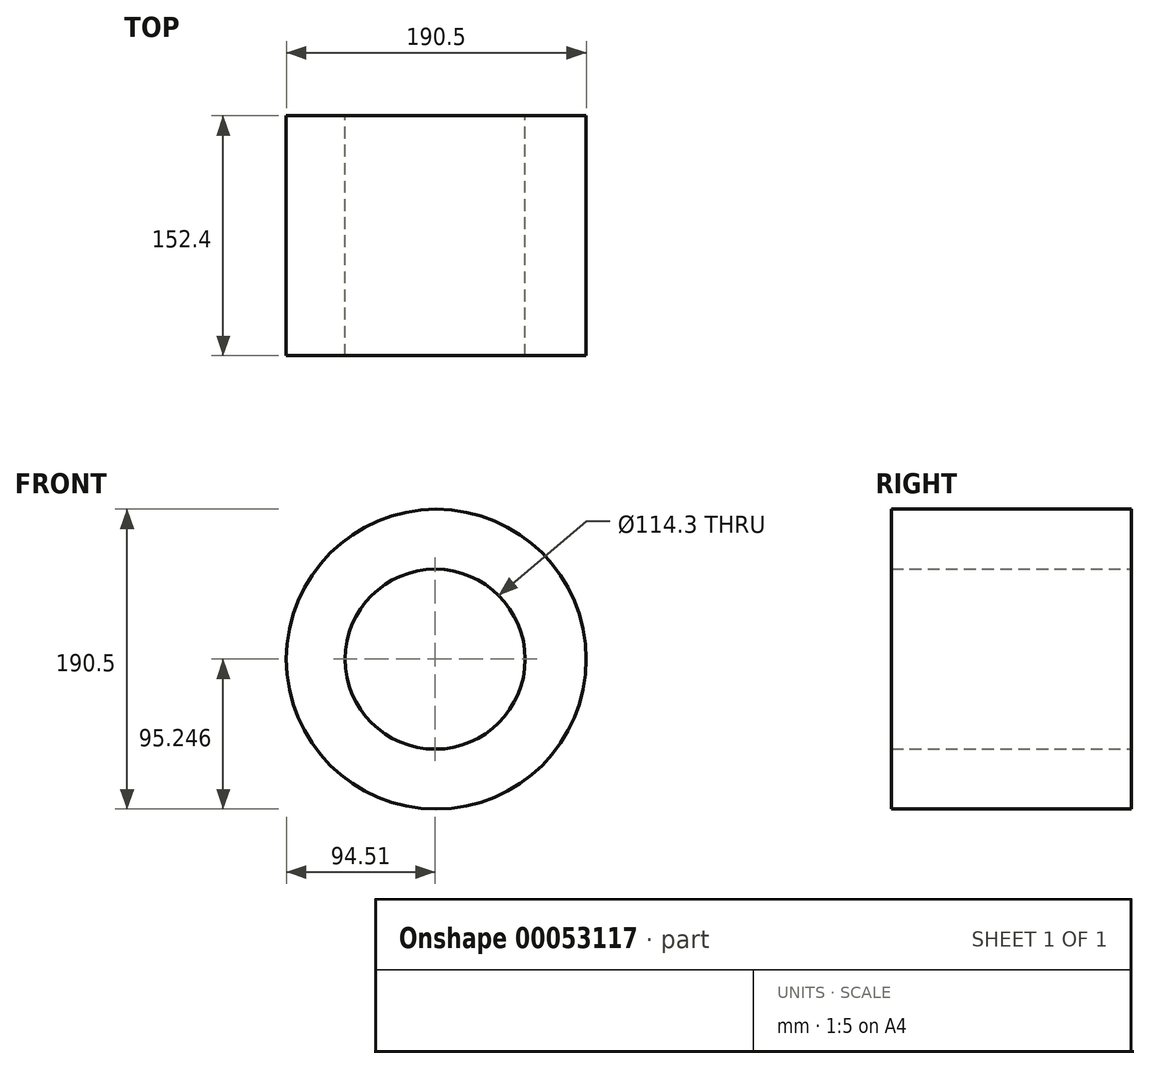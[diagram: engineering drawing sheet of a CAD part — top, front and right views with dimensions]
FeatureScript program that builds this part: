
annotation { "Feature Type Name" : "Feature", "Feature Type Description" : "" }
export const myFeature = defineFeature(function(context is Context, id is Id, definition is map)
    precondition{}
    {
        {
            var Q0;
            Q0=qCreatedBy(makeId("Front.planeOp"),FACE);
            var sketch = newSketch(context, id + "F0", { "sketchPlane" : qUnion([Q0])});
            skCircle(sketch, "E0", {"center": v(-0.38, -0.71) * mm, "radius": 57.15 * mm});
            skCircle(sketch, "E1", {"center": v(0.36, -0.71) * mm, "radius": 95.25 * mm});
            skSolve(sketch);
        }
        {
            var Q0;
            Q0=makeQuery(id+"F0.imprint","IMPRINT",FACE,{"disambiguationData":[TD([[makeQuery(id+"F0.imprint","IMPRINT",EDGE,{"derivedFrom":sQuery(id+"F0.wireOp",EDGE,"E0")}),-1.0]])]});
            extrude(context, id + "F1", {"entities" : qUnion([Q0]), "depth" : 152.4 * mm});
        }
    });
